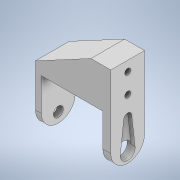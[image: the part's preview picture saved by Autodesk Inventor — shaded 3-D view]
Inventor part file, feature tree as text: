
AUTODESK INVENTOR PART (.ipt)
format: ipt  version: 2022.1 (Build 261234000, 234)  size: 172,032 bytes
history: native  units: mm
features: extrude x5, sketch x5, fillet x1
ambient origin geometry x8: Origin, YZ Plane, XZ Plane, XY Plane, X Axis, Y Axis, Z Axis, Center Point
bodies: Solid1 (feature_tree)
feature tree (11):
  extrude  "Extrusion1"  Depth=25.0mm
  extrude  "Extrusion2"  Depth=25.0mm
  extrude  "Extrusion3"  Depth=38.0mm
  fillet  "Fillet1"  Radius=20.0mm
  extrude  "Extrusion4"  Depth=17.0mm TaperAngle=0.0deg
  extrude  "Extrusion5"  Depth=3.0mm
  sketch  "Sketch1"  dims[d0=3.0mm d1=25.0mm]
  sketch  "Sketch2"  dims[d2=4.0mm d3=25.0mm]
  sketch  "Sketch3"  dims[d4=31.0mm d5=38.0mm d6=20.0mm]
  sketch  "Sketch4"  dims[d7=5.0mm d8=17.0mm d9=0.0mm]
  sketch  "Sketch5"  dims[d10=10.0mm d11=3.0mm d12=3.0mm d13=5.0mm d15=8.5mm d16=5.0mm d17=10.0mm d18=0.0mm d19=17.0mm d20=8.5mm d21=20.0mm d22=7.5mm d23=5.0mm d24=8.5mm d25=10.0mm d26=0.0mm d27=8.5mm d28=5.0mm d29=5.0mm d30=8.5mm d31=10.0mm d32=0.0mm d33=4.0mm d34=15.0mm d35=0.0mm d36=2.0mm d37=0.0mm]
